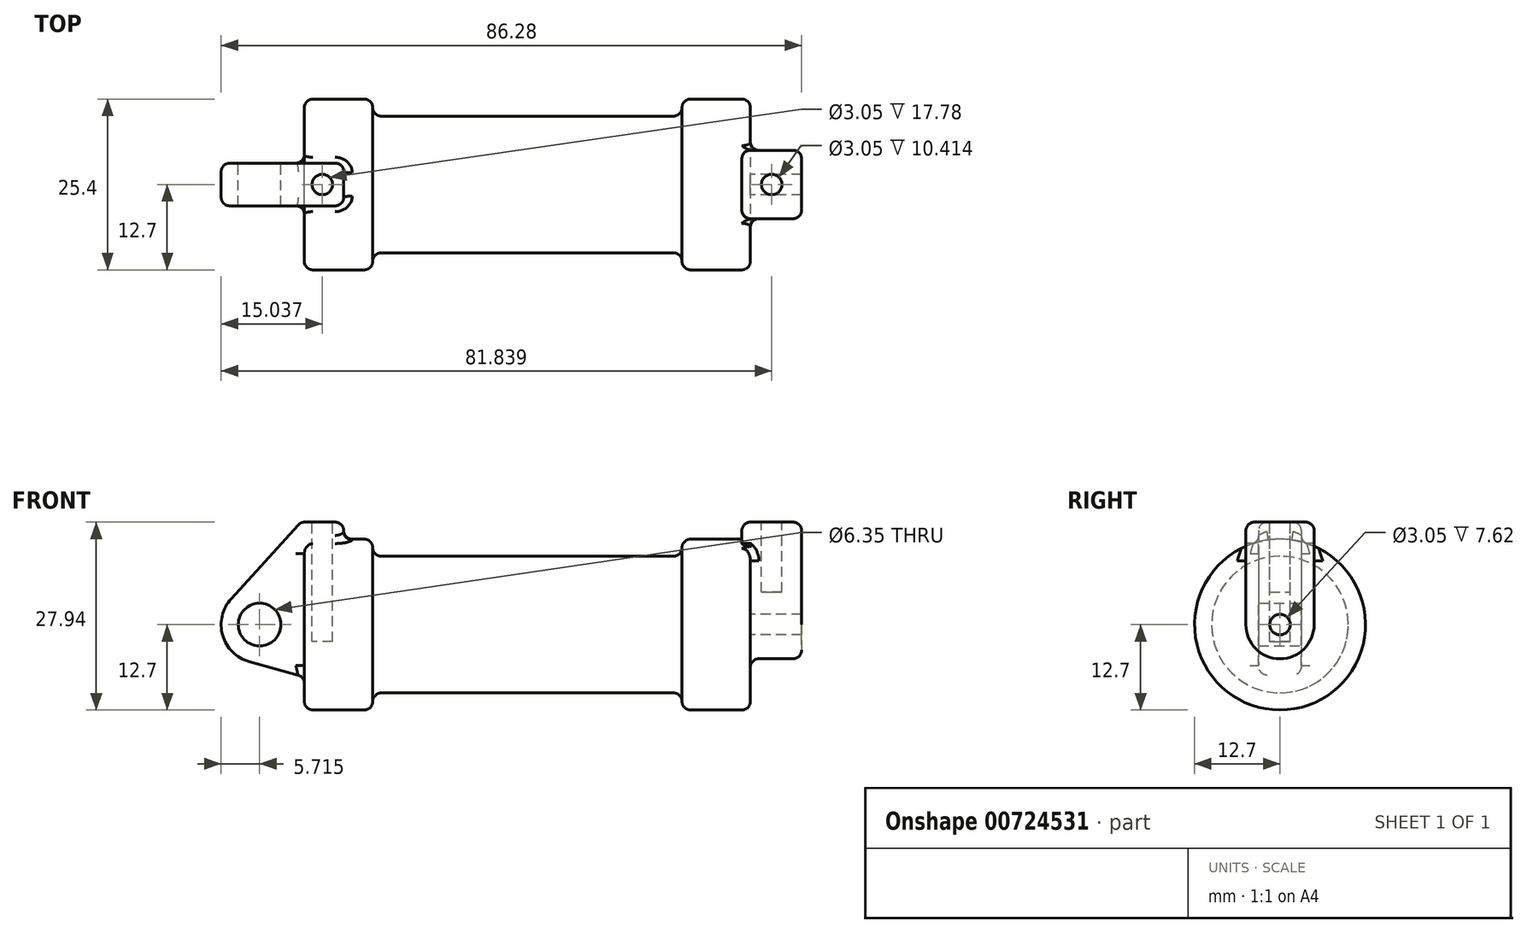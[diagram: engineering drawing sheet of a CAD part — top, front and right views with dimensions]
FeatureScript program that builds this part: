
annotation { "Feature Type Name" : "Feature", "Feature Type Description" : "" }
export const myFeature = defineFeature(function(context is Context, id is Id, definition is map)
    precondition{}
    {
        {
            var Q0;
            Q0=qCreatedBy(makeId("Front.planeOp"),FACE);
            var sketch = newSketch(context, id + "F0", { "sketchPlane" : qUnion([Q0])});
            skLineSegment(sketch, "E0", {"start": v(0, 0) * mm, "end": v(0, 12.7) * mm});
            skLineSegment(sketch, "E1", {"start": v(0, 12.7) * mm, "end": v(10.16, 12.7) * mm});
            skLineSegment(sketch, "E2", {"start": v(10.16, 12.7) * mm, "end": v(10.16, 10.16) * mm});
            skLineSegment(sketch, "E3", {"start": v(10.16, 10.16) * mm, "end": v(56.13, 10.16) * mm});
            skLineSegment(sketch, "E4", {"start": v(56.13, 10.16) * mm, "end": v(56.13, 12.7) * mm});
            skLineSegment(sketch, "E5", {"start": v(56.13, 12.7) * mm, "end": v(66.3, 12.7) * mm});
            skLineSegment(sketch, "E6", {"start": v(66.3, 12.7) * mm, "end": v(66.3, 0) * mm});
            skLineSegment(sketch, "E7", {"start": v(66.3, 0) * mm, "end": v(0, 0) * mm});
            skLineSegment(sketch, "E8", {"start": v(5.84, 15.24) * mm, "end": v(-0.5, 15.24) * mm});
            skLineSegment(sketch, "E9", {"start": v(-0.5, 15.24) * mm, "end": v(-10.88, 3.85) * mm});
            skLineSegment(sketch, "E10", {"start": v(0, 0) * mm, "end": v(-6.65, 0) * mm});
            skCircle(sketch, "E11", {"center": v(-6.65, 0) * mm, "radius": 5.72 * mm});
            skCircle(sketch, "E12", {"center": v(-6.65, 0) * mm, "radius": 3.18 * mm});
            skLineSegment(sketch, "E13", {"start": v(5.84, 15.24) * mm, "end": v(5.84, -9.4) * mm});
            skLineSegment(sketch, "E14", {"start": v(5.84, -9.4) * mm, "end": v(-8.18, -5.5) * mm});
            skSolve(sketch);
        }
        {
            var Q0;
            {var subQ0=sQuery(id+"F0.wireOp",EDGE,"E2");Q0=makeQuery(id+"F0.imprint","IMPRINT",FACE,{"disambiguationData":[TD([[makeQuery(id+"F0.imprint","IMPRINT",EDGE,{"derivedFrom":subQ0}),-1.0]])]});}
            var Q1;
            {var subQ0=sQuery(id+"F0.wireOp",EDGE,"E0");Q1=makeQuery(id+"F0.imprint","IMPRINT",FACE,{"disambiguationData":[TD([[makeQuery(id+"F0.imprint","IMPRINT",EDGE,{"derivedFrom":subQ0}),-1.0]])]});}
            var Q2;
            Q2=sQuery(id+"F0.wireOp",EDGE,"E7");
            revolve(context, id + "F1", {"entities" : qUnion([Q0, Q1]), "axis" : qUnion([Q2]), "revolveType" : RevolveType.FULL});
        }
        {
            var Q0;
            {var subQ1=sQuery(id+"F0.wireOp",EDGE,"E0");Q0=makeQuery(id+"F0.imprint","IMPRINT",FACE,{"disambiguationData":[TD([[makeQuery(id+"F0.imprint","IMPRINT",EDGE,{"derivedFrom":subQ1}),1.0]])]});}
            var Q1;
            {var subQ5=sQuery(id+"F0.wireOp",EDGE,"E12");Q1=makeQuery(id+"F0.imprint","IMPRINT",FACE,{"disambiguationData":[TD([[makeQuery(id+"F0.imprint","IMPRINT",EDGE,{"derivedFrom":subQ5}),-1.0]])]});}
            var Q2;
            {var subQ0=sQuery(id+"F0.wireOp",EDGE,"E14");Q2=makeQuery(id+"F0.imprint","IMPRINT",FACE,{"disambiguationData":[TD([[makeQuery(id+"F0.imprint","IMPRINT",EDGE,{"derivedFrom":subQ0}),-1.0]])]});}
            var Q3;
            {var subQ0=sQuery(id+"F0.wireOp",EDGE,"E0");Q3=makeQuery(id+"F0.imprint","IMPRINT",FACE,{"disambiguationData":[TD([[makeQuery(id+"F0.imprint","IMPRINT",EDGE,{"derivedFrom":subQ0}),-1.0]])]});}
            extrude(context, id + "F2", {"entities" : qUnion([Q0, Q1, Q2, Q3]), "operationType" : NewBodyOperationType.ADD, "endBound" : BoundingType.SYMMETRIC, "depth" : 6.35 * mm});
        }
        {
            var Q0;
            Q0=makeQuery(id+"F1.opRevolve","SWEPT_FACE",FACE,{"disambiguationData":[OSD([sQuery(id+"F0.wireOp",EDGE,"E6")])]});
            var sketch = newSketch(context, id + "F3", { "sketchPlane" : qUnion([Q0])});
            skLineSegment(sketch, "E15", {"start": v(-5.08, 15.23) * mm, "end": v(5.08, 15.23) * mm});
            skLineSegment(sketch, "E16", {"start": v(5.08, 15.23) * mm, "end": v(5.08, -0.01) * mm});
            skLineSegment(sketch, "E17", {"start": v(5.08, -0.01) * mm, "end": v(-5.08, -0.01) * mm});
            skLineSegment(sketch, "E18", {"start": v(-5.08, -0.01) * mm, "end": v(-5.08, 15.23) * mm});
            skCircle(sketch, "E19", {"center": v(0, 0) * mm, "radius": 5.08 * mm});
            skCircle(sketch, "E20", {"center": v(0, 0) * mm, "radius": 1.52 * mm});
            skLineSegment(sketch, "E21.MirrorCS", {"start": v(-5.08, 15.23) * mm, "end": v(-5.08, -0.01) * mm});
            skSolve(sketch);
        }
        {
            var Q0;
            {var subQ0=sQuery(id+"F3.wireOp",EDGE,"E19");var subQ1=sQuery(id+"F3.wireOp",EDGE,"E16");var subQ2=makeQuery(id+"F3.imprint","INTERSECT",VERTEX,{"derivedFrom":[subQ1,subQ0]});Q0=makeQuery(id+"F3.imprint","IMPRINT",FACE,{"disambiguationData":[TD([[makeQuery(id+"F3.imprint","IMPRINT",EDGE,{"disambiguationData":[TD([[subQ2,-1.0]])],"derivedFrom":subQ0}),-1.0]])]});}
            var Q1;
            {var subQ0=sQuery(id+"F3.wireOp",EDGE,"E19");var subQ2=sQuery(id+"F3.wireOp",EDGE,"E17");var subQ3=makeQuery(id+"F3.imprint","INTERSECT",VERTEX,{"derivedFrom":[subQ2,subQ0]});Q1=makeQuery(id+"F3.imprint","IMPRINT",FACE,{"disambiguationData":[TD([[makeQuery(id+"F3.imprint","IMPRINT",EDGE,{"disambiguationData":[TD([[subQ3,-1.0]])],"derivedFrom":subQ2}),-1.0]])]});}
            var Q2;
            {var subQ0=sQuery(id+"F3.wireOp",EDGE,"E19");var subQ1=sQuery(id+"F3.wireOp",EDGE,"E17");var subQ2=makeQuery(id+"F3.imprint","INTERSECT",VERTEX,{"derivedFrom":[subQ1,subQ0]});Q2=makeQuery(id+"F3.imprint","IMPRINT",FACE,{"disambiguationData":[TD([[makeQuery(id+"F3.imprint","IMPRINT",EDGE,{"disambiguationData":[TD([[subQ2,-1.0]])],"derivedFrom":subQ1}),1.0]])]});}
            var Q3;
            {var subQ0=sQuery(id+"F3.wireOp",EDGE,"E15");Q3=makeQuery(id+"F3.imprint","IMPRINT",FACE,{"disambiguationData":[TD([[makeQuery(id+"F3.imprint","IMPRINT",EDGE,{"derivedFrom":subQ0}),-1.0]])]});}
            extrude(context, id + "F4", {"entities" : qUnion([Q0, Q1, Q2, Q3]), "operationType" : NewBodyOperationType.ADD, "depth" : 7.62 * mm});
        }
        {
            var Q0;
            Q0=makeQuery(id+"F4.opExtrude","CAP_FACE",FACE,{"disambiguationData":[OSD([sQuery(id+"F3.wireOp",EDGE,"E15"),sQuery(id+"F3.wireOp",EDGE,"E16"),sQuery(id+"F3.wireOp",EDGE,"E19"),sQuery(id+"F3.wireOp",EDGE,"E20"),sQuery(id+"F3.wireOp",EDGE,"E21.MirrorCS")])],"isStart":true});
            extrude(context, id + "F5", {"entities" : qUnion([Q0]), "operationType" : NewBodyOperationType.ADD, "depth" : 1.27 * mm});
        }
        {
            var Q0;
            Q0=makeQuery(id+"F2.opExtrude","SWEPT_FACE",FACE,{"disambiguationData":[OSD([sQuery(id+"F0.wireOp",EDGE,"E8")])]});
            var sketch = newSketch(context, id + "F6", { "sketchPlane" : qUnion([Q0])});
            skLineSegment(sketch, "E22", {"start": v(2.67, 3.18) * mm, "end": v(2.67, -3.18) * mm, "construction": true});
            skLineSegment(sketch, "E23", {"start": v(-0.5, 0) * mm, "end": v(5.84, 0) * mm, "construction": true});
            skCircle(sketch, "E24", {"center": v(2.67, 0) * mm, "radius": 1.52 * mm});
            skSolve(sketch);
        }
        {
            var Q0;
            Q0=makeQuery(id+"F6.imprint","IMPRINT",FACE,{"disambiguationData":[TD([[makeQuery(id+"F6.imprint","IMPRINT",EDGE,{"derivedFrom":sQuery(id+"F6.wireOp",EDGE,"E24")}),1.0]])]});
            extrude(context, id + "F7", {"entities" : qUnion([Q0]), "operationType" : NewBodyOperationType.REMOVE, "oppositeDirection" : true, "depth" : 17.78 * mm});
        }
        {
            var Q0;
            {var subQ0=sQuery(id+"F3.wireOp",EDGE,"E15");Q0=makeQuery(id+"F5.boolean.opBoolean","MERGE",FACE,{"derivedFrom":[makeQuery(id+"F4.opExtrude","SWEPT_FACE",FACE,{"disambiguationData":[OSD([subQ0])]}),makeQuery(id+"F5.opExtrude","SWEPT_FACE",FACE,{"disambiguationData":[OSD([subQ0])]})]});}
            var sketch = newSketch(context, id + "F8", { "sketchPlane" : qUnion([Q0])});
            skLineSegment(sketch, "E25", {"start": v(65.02, 0) * mm, "end": v(73.91, 0) * mm});
            skCircle(sketch, "E26", {"center": v(69.47, 0) * mm, "radius": 1.52 * mm});
            skSolve(sketch);
        }
        {
            var Q0;
            {var subQ0=sQuery(id+"F8.wireOp",EDGE,"E26");var subQ1=sQuery(id+"F8.wireOp",EDGE,"E25");var subQ2=makeQuery(id+"F8.imprint","INTERSECT",VERTEX,{"disambiguationData":[OD(0.0)],"derivedFrom":[subQ1,subQ0]});Q0=makeQuery(id+"F8.imprint","IMPRINT",FACE,{"disambiguationData":[TD([[makeQuery(id+"F8.imprint","IMPRINT",EDGE,{"disambiguationData":[TD([[subQ2,-1.0]])],"derivedFrom":subQ1}),1.0]])]});}
            var Q1;
            {var subQ0=sQuery(id+"F8.wireOp",EDGE,"E26");var subQ1=sQuery(id+"F8.wireOp",EDGE,"E25");var subQ2=makeQuery(id+"F8.imprint","INTERSECT",VERTEX,{"disambiguationData":[OD(0.0)],"derivedFrom":[subQ1,subQ0]});Q1=makeQuery(id+"F8.imprint","IMPRINT",FACE,{"disambiguationData":[TD([[makeQuery(id+"F8.imprint","IMPRINT",EDGE,{"disambiguationData":[TD([[subQ2,-1.0]])],"derivedFrom":subQ1}),-1.0]])]});}
            extrude(context, id + "F9", {"entities" : qUnion([Q0, Q1]), "operationType" : NewBodyOperationType.REMOVE, "oppositeDirection" : true, "depth" : 10.4 * mm});
        }
        {
            var Q0;
            {var subQ0=sQuery(id+"F0.wireOp",EDGE,"E5");var subQ1=sQuery(id+"F0.wireOp",EDGE,"E6");Q0=makeQuery(id+"F4.boolean.opBoolean","SPLIT",EDGE,{"disambiguationData":[topologyDisambiguationEdgeConnected([makeQuery(id+"F1.opRevolve","SWEPT_FACE",FACE,{"disambiguationData":[OSD([subQ1])]})])],"derivedFrom":makeQuery(id+"F1.opRevolve","SWEPT_EDGE",EDGE,{"disambiguationData":[OSD([subQ0,subQ1])]})});}
            var Q1;
            Q1=makeQuery(id+"F1.opRevolve","SWEPT_EDGE",EDGE,{"disambiguationData":[OSD([sQuery(id+"F0.wireOp",EDGE,"E4"),sQuery(id+"F0.wireOp",EDGE,"E5")])]});
            var Q2;
            Q2=makeQuery(id+"F1.opRevolve","SWEPT_EDGE",EDGE,{"disambiguationData":[OSD([sQuery(id+"F0.wireOp",EDGE,"E1"),sQuery(id+"F0.wireOp",EDGE,"E2")])]});
            var Q3;
            Q3=makeQuery(id+"F1.opRevolve","SWEPT_EDGE",EDGE,{"disambiguationData":[OSD([sQuery(id+"F0.wireOp",EDGE,"E2"),sQuery(id+"F0.wireOp",EDGE,"E3")])]});
            var Q4;
            Q4=makeQuery(id+"F1.opRevolve","SWEPT_EDGE",EDGE,{"disambiguationData":[OSD([sQuery(id+"F0.wireOp",EDGE,"E0"),sQuery(id+"F0.wireOp",EDGE,"E1")])]});
            var Q5;
            Q5=makeQuery(id+"F1.opRevolve","SWEPT_EDGE",EDGE,{"disambiguationData":[OSD([sQuery(id+"F0.wireOp",EDGE,"E3"),sQuery(id+"F0.wireOp",EDGE,"E4")])]});
            fillet(context, id + "F10", {"entities" : qUnion([Q0, Q1, Q2, Q3, Q4, Q5]), "radius" : 1.27 * mm, "tangentPropagation" : true, "allowEdgeOverflow" : false});
        }
        {
            var Q0;
            Q0=makeQuery(id+"F4.opExtrude","CAP_EDGE",EDGE,{"disambiguationData":[OSD([sQuery(id+"F3.wireOp",EDGE,"E15")])],"isStart":false});
            var Q1;
            Q1=makeQuery(id+"F4.opExtrude","SWEPT_EDGE",EDGE,{"disambiguationData":[OSD([sQuery(id+"F3.wireOp",EDGE,"E15"),sQuery(id+"F3.wireOp",EDGE,"E21.MirrorCS")])]});
            var Q2;
            Q2=makeQuery(id+"F4.opExtrude","CAP_EDGE",EDGE,{"disambiguationData":[OSD([sQuery(id+"F3.wireOp",EDGE,"E21.MirrorCS")])],"isStart":false});
            var Q3;
            Q3=makeQuery(id+"F4.opExtrude","CAP_EDGE",EDGE,{"disambiguationData":[OSD([sQuery(id+"F3.wireOp",EDGE,"E16")])],"isStart":false});
            var Q4;
            Q4=makeQuery(id+"F4.opExtrude","CAP_EDGE",EDGE,{"disambiguationData":[OSD([sQuery(id+"F3.wireOp",EDGE,"E19")])],"isStart":false});
            var Q5;
            Q5=makeQuery(id+"F4.opExtrude","CAP_EDGE",EDGE,{"disambiguationData":[OSD([sQuery(id+"F3.wireOp",EDGE,"E19")])],"isStart":true});
            var Q6;
            {var subQ0=sQuery(id+"F3.wireOp",EDGE,"E16");Q6=makeQuery(id+"F4.boolean.opBoolean","SPLIT",EDGE,{"disambiguationData":[topologyDisambiguationEdgeConnected([makeQuery(id+"F1.opRevolve","SWEPT_FACE",FACE,{"disambiguationData":[OSD([sQuery(id+"F0.wireOp",EDGE,"E6")])]})])],"derivedFrom":makeQuery(id+"F4.opExtrude","CAP_EDGE",EDGE,{"disambiguationData":[OSD([subQ0])],"isStart":true})});}
            var Q7;
            Q7=makeQuery(id+"F5.opExtrude","SWEPT_EDGE",EDGE,{"disambiguationData":[OSD([sQuery(id+"F3.wireOp",EDGE,"E15"),sQuery(id+"F3.wireOp",EDGE,"E21.MirrorCS")])]});
            var Q8;
            Q8=makeQuery(id+"F10.opFillet","BLEND_FACE",FACE,{"disambiguationData":[OSD([sQuery(id+"F0.wireOp",EDGE,"E5"),sQuery(id+"F0.wireOp",EDGE,"E6")])]});
            var Q9;
            {var subQ0=sQuery(id+"F3.wireOp",EDGE,"E21.MirrorCS");var subQ1=sQuery(id+"F0.wireOp",EDGE,"E5");var subQ2=sQuery(id+"F0.wireOp",EDGE,"E6");Q9=makeQuery(id+"F10.opFillet","BLEND_EDGE",EDGE,{"blendedFrom":[makeQuery(id+"F4.boolean.opBoolean","SPLIT",EDGE,{"disambiguationData":[topologyDisambiguationEdgeConnected([makeQuery(id+"F1.opRevolve","SWEPT_FACE",FACE,{"disambiguationData":[OSD([subQ2])]})])],"derivedFrom":makeQuery(id+"F1.opRevolve","SWEPT_EDGE",EDGE,{"disambiguationData":[OSD([subQ1,subQ2])]})}),makeQuery(id+"F5.boolean.opBoolean","MERGE",FACE,{"derivedFrom":[makeQuery(id+"F4.opExtrude","SWEPT_FACE",FACE,{"disambiguationData":[OSD([subQ0])]}),makeQuery(id+"F5.opExtrude","SWEPT_FACE",FACE,{"disambiguationData":[OSD([subQ0])]})]})],"blendedInto":[makeQuery(id+"F5.boolean.opBoolean","MERGE",FACE,{"derivedFrom":[makeQuery(id+"F4.opExtrude","SWEPT_FACE",FACE,{"disambiguationData":[OSD([subQ0])]}),makeQuery(id+"F5.opExtrude","SWEPT_FACE",FACE,{"disambiguationData":[OSD([subQ0])]})]})]});}
            var Q10;
            Q10=makeQuery(id+"F5.opExtrude","CAP_EDGE",EDGE,{"disambiguationData":[OSD([sQuery(id+"F3.wireOp",EDGE,"E15")])],"isStart":false});
            var Q11;
            {var subQ0=sQuery(id+"F3.wireOp",EDGE,"E16");var subQ1=sQuery(id+"F3.wireOp",EDGE,"E15");Q11=makeQuery(id+"F5.boolean.opBoolean","MERGE",EDGE,{"derivedFrom":[makeQuery(id+"F4.opExtrude","SWEPT_EDGE",EDGE,{"disambiguationData":[OSD([subQ1,subQ0])]}),makeQuery(id+"F5.opExtrude","SWEPT_EDGE",EDGE,{"disambiguationData":[OSD([subQ1,subQ0])]})]});}
            var Q12;
            {var subQ0=sQuery(id+"F3.wireOp",EDGE,"E21.MirrorCS");Q12=makeQuery(id+"F4.boolean.opBoolean","SPLIT",EDGE,{"disambiguationData":[topologyDisambiguationEdgeConnected([makeQuery(id+"F1.opRevolve","SWEPT_FACE",FACE,{"disambiguationData":[OSD([sQuery(id+"F0.wireOp",EDGE,"E6")])]})])],"derivedFrom":makeQuery(id+"F4.opExtrude","CAP_EDGE",EDGE,{"disambiguationData":[OSD([subQ0])],"isStart":true})});}
            var Q13;
            {var subQ0=sQuery(id+"F3.wireOp",EDGE,"E16");var subQ1=sQuery(id+"F0.wireOp",EDGE,"E5");var subQ2=sQuery(id+"F0.wireOp",EDGE,"E6");Q13=makeQuery(id+"F10.opFillet","BLEND_EDGE",EDGE,{"blendedFrom":[makeQuery(id+"F4.boolean.opBoolean","SPLIT",EDGE,{"disambiguationData":[topologyDisambiguationEdgeConnected([makeQuery(id+"F1.opRevolve","SWEPT_FACE",FACE,{"disambiguationData":[OSD([subQ2])]})])],"derivedFrom":makeQuery(id+"F1.opRevolve","SWEPT_EDGE",EDGE,{"disambiguationData":[OSD([subQ1,subQ2])]})}),makeQuery(id+"F5.boolean.opBoolean","MERGE",FACE,{"derivedFrom":[makeQuery(id+"F4.opExtrude","SWEPT_FACE",FACE,{"disambiguationData":[OSD([subQ0])]}),makeQuery(id+"F5.opExtrude","SWEPT_FACE",FACE,{"disambiguationData":[OSD([subQ0])]})]})],"blendedInto":[makeQuery(id+"F5.boolean.opBoolean","MERGE",FACE,{"derivedFrom":[makeQuery(id+"F4.opExtrude","SWEPT_FACE",FACE,{"disambiguationData":[OSD([subQ0])]}),makeQuery(id+"F5.opExtrude","SWEPT_FACE",FACE,{"disambiguationData":[OSD([subQ0])]})]})]});}
            fillet(context, id + "F11", {"entities" : qUnion([Q0, Q1, Q2, Q3, Q4, Q5, Q6, Q7, Q8, Q9, Q10, Q11, Q12, Q13]), "radius" : 1.27 * mm, "tangentPropagation" : true, "allowEdgeOverflow" : false});
        }
        {
            var Q0;
            Q0=makeQuery(id+"F5.opExtrude","CAP_EDGE",EDGE,{"disambiguationData":[OSD([sQuery(id+"F3.wireOp",EDGE,"E16")])],"isStart":false});
            var Q1;
            Q1=makeQuery(id+"F5.opExtrude","CAP_EDGE",EDGE,{"disambiguationData":[OSD([sQuery(id+"F3.wireOp",EDGE,"E21.MirrorCS")])],"isStart":false});
            var Q2;
            Q2=makeQuery(id+"F2.boolean.opBoolean","INTERSECT",EDGE,{"derivedFrom":[makeQuery(id+"F1.opRevolve","SWEPT_FACE",FACE,{"disambiguationData":[OSD([sQuery(id+"F0.wireOp",EDGE,"E1")])]}),makeQuery(id+"F2.opExtrude","CAP_FACE",FACE,{"disambiguationData":[OSD([sQuery(id+"F0.wireOp",EDGE,"E8"),sQuery(id+"F0.wireOp",EDGE,"E9"),sQuery(id+"F0.wireOp",EDGE,"E11"),sQuery(id+"F0.wireOp",EDGE,"E12"),sQuery(id+"F0.wireOp",EDGE,"E13"),sQuery(id+"F0.wireOp",EDGE,"E14")])],"isStart":true})]});
            var Q3;
            Q3=makeQuery(id+"F2.boolean.opBoolean","INTERSECT",EDGE,{"derivedFrom":[makeQuery(id+"F1.opRevolve","SWEPT_FACE",FACE,{"disambiguationData":[OSD([sQuery(id+"F0.wireOp",EDGE,"E0")])]}),makeQuery(id+"F2.opExtrude","CAP_FACE",FACE,{"disambiguationData":[OSD([sQuery(id+"F0.wireOp",EDGE,"E8"),sQuery(id+"F0.wireOp",EDGE,"E9"),sQuery(id+"F0.wireOp",EDGE,"E11"),sQuery(id+"F0.wireOp",EDGE,"E12"),sQuery(id+"F0.wireOp",EDGE,"E13"),sQuery(id+"F0.wireOp",EDGE,"E14")])],"isStart":true})]});
            var Q4;
            Q4=makeQuery(id+"F10.opFillet","BLEND_EDGE",EDGE,{"blendedFrom":[makeQuery(id+"F1.opRevolve","SWEPT_EDGE",EDGE,{"disambiguationData":[OSD([sQuery(id+"F0.wireOp",EDGE,"E0"),sQuery(id+"F0.wireOp",EDGE,"E1")])]}),makeQuery(id+"F2.opExtrude","CAP_FACE",FACE,{"disambiguationData":[OSD([sQuery(id+"F0.wireOp",EDGE,"E8"),sQuery(id+"F0.wireOp",EDGE,"E9"),sQuery(id+"F0.wireOp",EDGE,"E11"),sQuery(id+"F0.wireOp",EDGE,"E12"),sQuery(id+"F0.wireOp",EDGE,"E13"),sQuery(id+"F0.wireOp",EDGE,"E14")])],"isStart":true})],"blendedInto":[makeQuery(id+"F2.opExtrude","CAP_FACE",FACE,{"disambiguationData":[OSD([sQuery(id+"F0.wireOp",EDGE,"E8"),sQuery(id+"F0.wireOp",EDGE,"E9"),sQuery(id+"F0.wireOp",EDGE,"E11"),sQuery(id+"F0.wireOp",EDGE,"E12"),sQuery(id+"F0.wireOp",EDGE,"E13"),sQuery(id+"F0.wireOp",EDGE,"E14")])],"isStart":true})]});
            var Q5;
            Q5=makeQuery(id+"F2.opExtrude","CAP_EDGE",EDGE,{"disambiguationData":[OSD([sQuery(id+"F0.wireOp",EDGE,"E9")])],"isStart":true});
            var Q6;
            Q6=makeQuery(id+"F2.opExtrude","CAP_EDGE",EDGE,{"disambiguationData":[OSD([sQuery(id+"F0.wireOp",EDGE,"E11")])],"isStart":true});
            var Q7;
            Q7=makeQuery(id+"F2.opExtrude","CAP_EDGE",EDGE,{"disambiguationData":[OSD([sQuery(id+"F0.wireOp",EDGE,"E14")])],"isStart":false});
            var Q8;
            Q8=makeQuery(id+"F2.opExtrude","CAP_EDGE",EDGE,{"disambiguationData":[OSD([sQuery(id+"F0.wireOp",EDGE,"E13")])],"isStart":true});
            var Q9;
            Q9=makeQuery(id+"F2.opExtrude","CAP_EDGE",EDGE,{"disambiguationData":[OSD([sQuery(id+"F0.wireOp",EDGE,"E8")])],"isStart":true});
            var Q10;
            Q10=makeQuery(id+"F2.opExtrude","SWEPT_EDGE",EDGE,{"disambiguationData":[OSD([sQuery(id+"F0.wireOp",EDGE,"E8"),sQuery(id+"F0.wireOp",EDGE,"E9")])]});
            var Q11;
            Q11=makeQuery(id+"F2.opExtrude","SWEPT_EDGE",EDGE,{"disambiguationData":[OSD([sQuery(id+"F0.wireOp",EDGE,"E8"),sQuery(id+"F0.wireOp",EDGE,"E13")])]});
            var Q12;
            Q12=makeQuery(id+"F2.opExtrude","CAP_EDGE",EDGE,{"disambiguationData":[OSD([sQuery(id+"F0.wireOp",EDGE,"E8")])],"isStart":false});
            var Q13;
            Q13=makeQuery(id+"F2.boolean.opBoolean","INTERSECT",EDGE,{"derivedFrom":[makeQuery(id+"F1.opRevolve","SWEPT_FACE",FACE,{"disambiguationData":[OSD([sQuery(id+"F0.wireOp",EDGE,"E1")])]}),makeQuery(id+"F2.opExtrude","CAP_FACE",FACE,{"disambiguationData":[OSD([sQuery(id+"F0.wireOp",EDGE,"E8"),sQuery(id+"F0.wireOp",EDGE,"E9"),sQuery(id+"F0.wireOp",EDGE,"E11"),sQuery(id+"F0.wireOp",EDGE,"E12"),sQuery(id+"F0.wireOp",EDGE,"E13"),sQuery(id+"F0.wireOp",EDGE,"E14")])],"isStart":false})]});
            var Q14;
            Q14=makeQuery(id+"F2.opExtrude","CAP_EDGE",EDGE,{"disambiguationData":[OSD([sQuery(id+"F0.wireOp",EDGE,"E13")])],"isStart":false});
            var Q15;
            Q15=makeQuery(id+"F2.opExtrude","CAP_EDGE",EDGE,{"disambiguationData":[OSD([sQuery(id+"F0.wireOp",EDGE,"E9")])],"isStart":false});
            var Q16;
            Q16=makeQuery(id+"F2.opExtrude","CAP_EDGE",EDGE,{"disambiguationData":[OSD([sQuery(id+"F0.wireOp",EDGE,"E11")])],"isStart":false});
            var Q17;
            Q17=makeQuery(id+"F10.opFillet","BLEND_EDGE",EDGE,{"blendedFrom":[makeQuery(id+"F1.opRevolve","SWEPT_EDGE",EDGE,{"disambiguationData":[OSD([sQuery(id+"F0.wireOp",EDGE,"E0"),sQuery(id+"F0.wireOp",EDGE,"E1")])]}),makeQuery(id+"F2.opExtrude","CAP_FACE",FACE,{"disambiguationData":[OSD([sQuery(id+"F0.wireOp",EDGE,"E8"),sQuery(id+"F0.wireOp",EDGE,"E9"),sQuery(id+"F0.wireOp",EDGE,"E11"),sQuery(id+"F0.wireOp",EDGE,"E12"),sQuery(id+"F0.wireOp",EDGE,"E13"),sQuery(id+"F0.wireOp",EDGE,"E14")])],"isStart":false})],"blendedInto":[makeQuery(id+"F2.opExtrude","CAP_FACE",FACE,{"disambiguationData":[OSD([sQuery(id+"F0.wireOp",EDGE,"E8"),sQuery(id+"F0.wireOp",EDGE,"E9"),sQuery(id+"F0.wireOp",EDGE,"E11"),sQuery(id+"F0.wireOp",EDGE,"E12"),sQuery(id+"F0.wireOp",EDGE,"E13"),sQuery(id+"F0.wireOp",EDGE,"E14")])],"isStart":false})]});
            var Q18;
            Q18=makeQuery(id+"F1.opRevolve","SWEPT_FACE",FACE,{"disambiguationData":[OSD([sQuery(id+"F0.wireOp",EDGE,"E1")])]});
            var Q19;
            Q19=makeQuery(id+"F2.opExtrude","SWEPT_FACE",FACE,{"disambiguationData":[OSD([sQuery(id+"F0.wireOp",EDGE,"E13")])]});
            var Q20;
            Q20=makeQuery(id+"F2.opExtrude","SWEPT_FACE",FACE,{"disambiguationData":[OSD([sQuery(id+"F0.wireOp",EDGE,"E14")])]});
            var Q21;
            {var subQ0=sQuery(id+"F3.wireOp",EDGE,"E15");Q21=makeQuery(id+"F11.opFillet","BLEND_EDGE",EDGE,{"blendedFrom":[makeQuery(id+"F5.opExtrude","CAP_EDGE",EDGE,{"disambiguationData":[OSD([subQ0])],"isStart":false}),makeQuery(id+"F5.opExtrude","CAP_FACE",FACE,{"disambiguationData":[OSD([subQ0,sQuery(id+"F3.wireOp",EDGE,"E16"),sQuery(id+"F3.wireOp",EDGE,"E19"),sQuery(id+"F3.wireOp",EDGE,"E20"),sQuery(id+"F3.wireOp",EDGE,"E21.MirrorCS")])],"isStart":false})],"blendedInto":[makeQuery(id+"F5.opExtrude","CAP_FACE",FACE,{"disambiguationData":[OSD([subQ0,sQuery(id+"F3.wireOp",EDGE,"E16"),sQuery(id+"F3.wireOp",EDGE,"E19"),sQuery(id+"F3.wireOp",EDGE,"E20"),sQuery(id+"F3.wireOp",EDGE,"E21.MirrorCS")])],"isStart":false})]});}
            fillet(context, id + "F12", {"entities" : qUnion([Q0, Q1, Q2, Q3, Q4, Q5, Q6, Q7, Q8, Q9, Q10, Q11, Q12, Q13, Q14, Q15, Q16, Q17, Q18, Q19, Q20, Q21]), "radius" : 1.27 * mm, "tangentPropagation" : true, "allowEdgeOverflow" : false});
        }
    });
